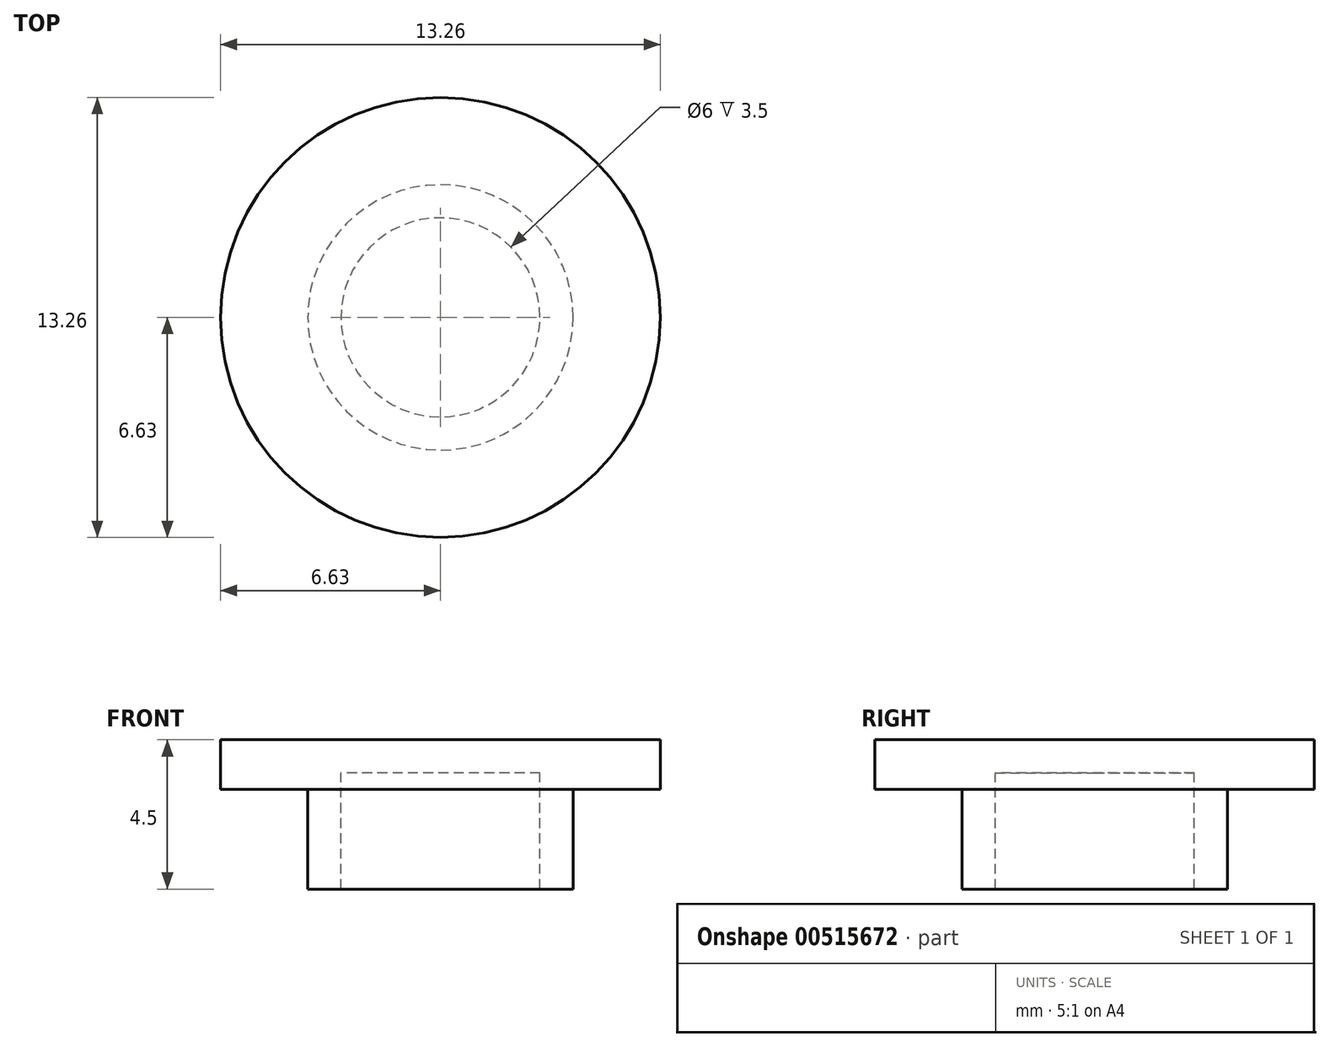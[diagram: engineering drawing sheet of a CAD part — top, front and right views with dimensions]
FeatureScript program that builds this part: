
annotation { "Feature Type Name" : "Feature", "Feature Type Description" : "" }
export const myFeature = defineFeature(function(context is Context, id is Id, definition is map)
    precondition{}
    {
        {
            var Q0;
            Q0=qCreatedBy(makeId("Top.planeOp"),FACE);
            var sketch = newSketch(context, id + "F0", { "sketchPlane" : qUnion([Q0])});
            skCircle(sketch, "E0", {"center": v(0, 0) * mm, "radius": 4 * mm});
            skCircle(sketch, "E1", {"center": v(0, 0) * mm, "radius": 6.62 * mm});
            skSolve(sketch);
        }
        {
            var Q0;
            Q0=makeQuery(id+"F0.imprint","IMPRINT",FACE,{"disambiguationData":[TD([[makeQuery(id+"F0.imprint","IMPRINT",EDGE,{"derivedFrom":sQuery(id+"F0.wireOp",EDGE,"E0")}),1.0]])]});
            var Q1;
            Q1=makeQuery(id+"F0.imprint","IMPRINT",FACE,{"disambiguationData":[TD([[makeQuery(id+"F0.imprint","IMPRINT",EDGE,{"derivedFrom":sQuery(id+"F0.wireOp",EDGE,"E0")}),-1.0]])]});
            extrude(context, id + "F1", {"entities" : qUnion([Q0, Q1]), "depth" : 1.5 * mm});
        }
        {
            var Q0;
            Q0=makeQuery(id+"F0.imprint","IMPRINT",FACE,{"disambiguationData":[TD([[makeQuery(id+"F0.imprint","IMPRINT",EDGE,{"derivedFrom":sQuery(id+"F0.wireOp",EDGE,"E0")}),1.0]])]});
            extrude(context, id + "F2", {"entities" : qUnion([Q0]), "operationType" : NewBodyOperationType.ADD, "oppositeDirection" : true, "depth" : 3 * mm, "offsetDistance" : 25 * mm});
        }
        {
            var Q0;
            Q0=makeQuery(id+"F2.opExtrude","CAP_FACE",FACE,{"disambiguationData":[OSD([sQuery(id+"F0.wireOp",EDGE,"E0")])],"isStart":false});
            shell(context, id + "F3", {"entities" : qUnion([Q0]), "thickness" : 1 * mm});
        }
    });
